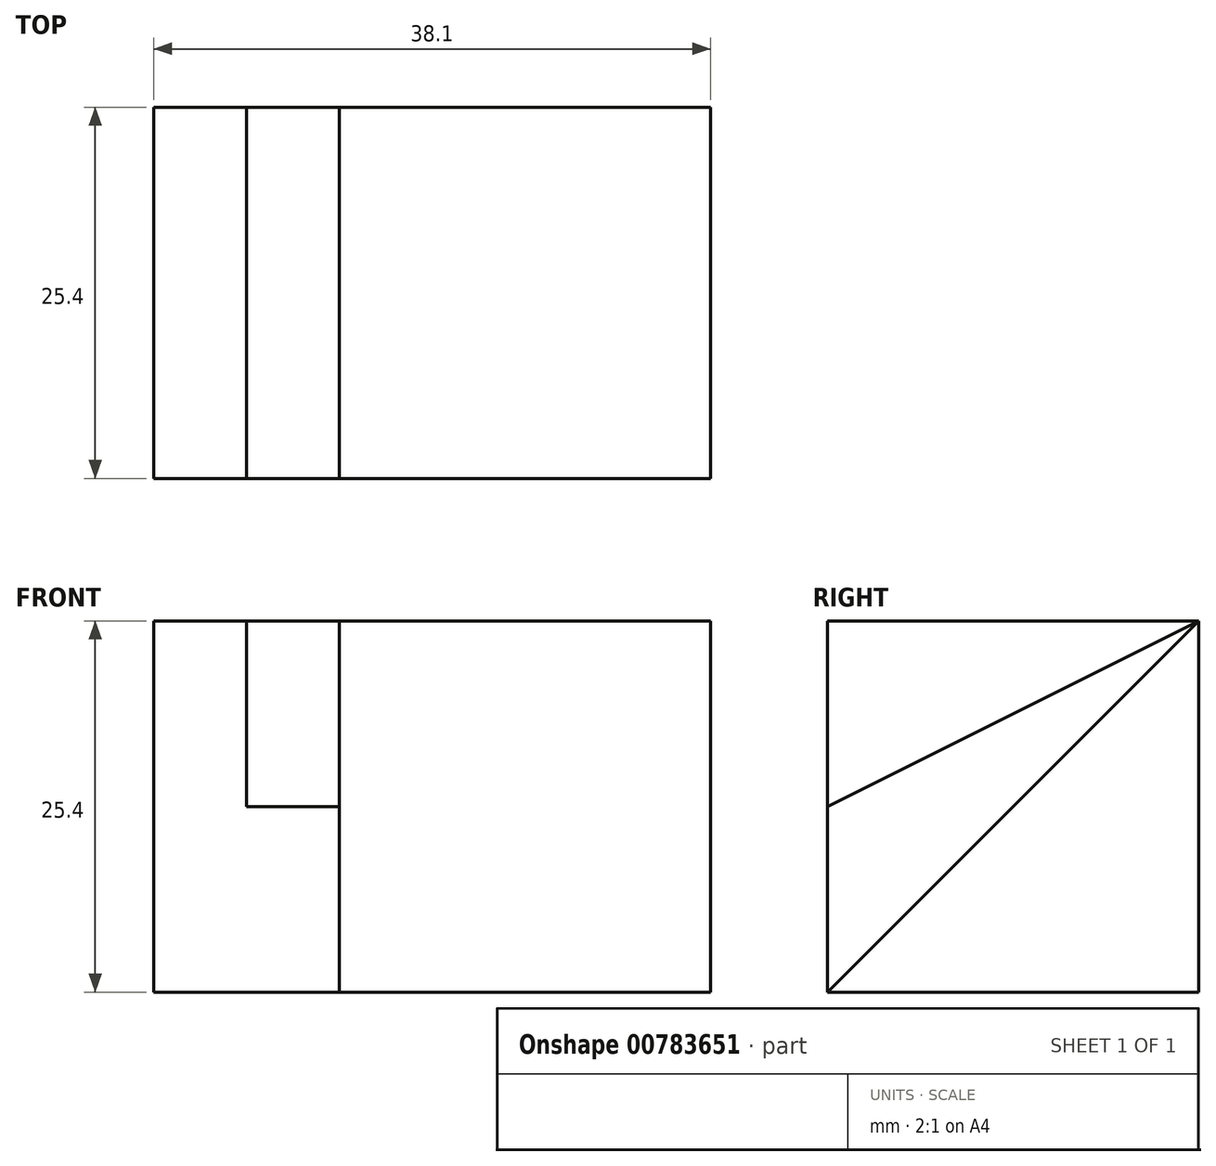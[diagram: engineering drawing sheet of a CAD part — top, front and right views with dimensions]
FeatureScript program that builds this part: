
annotation { "Feature Type Name" : "Feature", "Feature Type Description" : "" }
export const myFeature = defineFeature(function(context is Context, id is Id, definition is map)
    precondition{}
    {
        {
            var Q0;
            Q0=qCreatedBy(makeId("Front.planeOp"),FACE);
            var sketch = newSketch(context, id + "F0", { "sketchPlane" : qUnion([Q0])});
            skLineSegment(sketch, "E0", {"start": v(0, 0) * mm, "end": v(0, 25.4) * mm});
            skLineSegment(sketch, "E1", {"start": v(0, 25.4) * mm, "end": v(38.1, 25.4) * mm});
            skLineSegment(sketch, "E2", {"start": v(38.1, 25.4) * mm, "end": v(38.1, 0) * mm});
            skLineSegment(sketch, "E3", {"start": v(38.1, 0) * mm, "end": v(0, 0) * mm});
            skSolve(sketch);
        }
        {
            var Q0;
            Q0=makeQuery(id+"F0.imprint","IMPRINT",FACE,{"disambiguationData":[TD([[makeQuery(id+"F0.imprint","IMPRINT",EDGE,{"derivedFrom":sQuery(id+"F0.wireOp",EDGE,"E0")}),-1.0]])]});
            extrude(context, id + "F1", {"entities" : qUnion([Q0]), "depth" : 25.4 * mm, "offsetDistance" : 25.4 * mm});
        }
        {
            var Q0;
            Q0=makeQuery(id+"F1.opExtrude","SWEPT_FACE",FACE,{"disambiguationData":[OSD([sQuery(id+"F0.wireOp",EDGE,"E2")])]});
            var sketch = newSketch(context, id + "F2", { "sketchPlane" : qUnion([Q0])});
            skLineSegment(sketch, "E4", {"start": v(0, 25.4) * mm, "end": v(-25.4, 0) * mm});
            skSolve(sketch);
        }
        {
            var Q0;
            Q0=makeQuery(id+"F2.imprint","IMPRINT",FACE,{"disambiguationData":[TD([[makeQuery(id+"F2.imprint","IMPRINT",EDGE,{"derivedFrom":sQuery(id+"F2.wireOp",EDGE,"E4")}),-1.0]])]});
            extrude(context, id + "F3", {"entities" : qUnion([Q0]), "operationType" : NewBodyOperationType.REMOVE, "oppositeDirection" : true, "depth" : 25.4 * mm, "offsetDistance" : 25.4 * mm});
        }
        {
            var Q0;
            Q0=makeQuery(id+"F3.boolean.opBoolean","COPY",FACE,{"derivedFrom":makeQuery(id+"F3.opExtrude","CAP_FACE",FACE,{"disambiguationData":[OSD([sQuery(id+"F0.wireOp",EDGE,"E1"),sQuery(id+"F0.wireOp",EDGE,"E2"),sQuery(id+"F2.wireOp",EDGE,"E4")])],"isStart":false})});
            var sketch = newSketch(context, id + "F4", { "sketchPlane" : qUnion([Q0])});
            skLineSegment(sketch, "E5", {"start": v(-25.4, 0) * mm, "end": v(-25.4, 12.7) * mm});
            skLineSegment(sketch, "E6", {"start": v(-25.4, 12.7) * mm, "end": v(0, 25.4) * mm});
            skSolve(sketch);
        }
        {
            var Q0;
            {var subQ0=sQuery(id+"F4.wireOp",EDGE,"E6");Q0=makeQuery(id+"F4.imprint","IMPRINT",FACE,{"disambiguationData":[TD([[makeQuery(id+"F4.imprint","IMPRINT",EDGE,{"derivedFrom":subQ0}),1.0]])]});}
            extrude(context, id + "F5", {"entities" : qUnion([Q0]), "operationType" : NewBodyOperationType.REMOVE, "oppositeDirection" : true, "depth" : 6.35 * mm, "offsetDistance" : 25.4 * mm});
        }
    });
